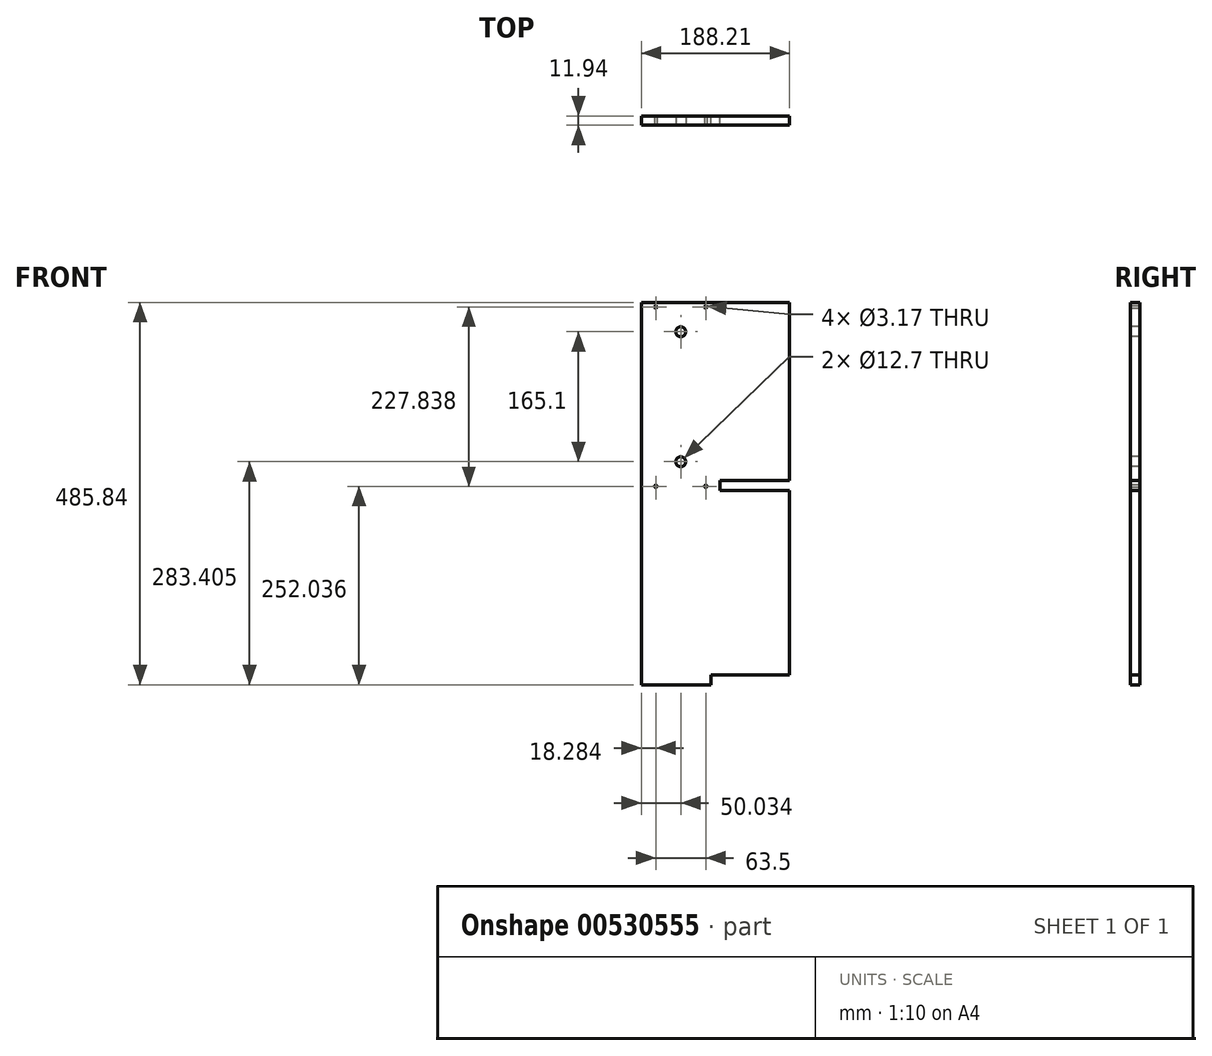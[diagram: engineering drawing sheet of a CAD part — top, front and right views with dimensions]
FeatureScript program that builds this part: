
annotation { "Feature Type Name" : "Feature", "Feature Type Description" : "" }
export const myFeature = defineFeature(function(context is Context, id is Id, definition is map)
    precondition{}
    {
        {
            var Q0;
            Q0=qCreatedBy(makeId("Front.planeOp"),FACE);
            var sketch = newSketch(context, id + "F0", { "sketchPlane" : qUnion([Q0])});
            skLineSegment(sketch, "E0", {"start": v(-136.42, 252.83) * mm, "end": v(-36.35, 252.83) * mm});
            skLineSegment(sketch, "E1", {"start": v(-36.35, 26.52) * mm, "end": v(-36.35, 13.82) * mm});
            skLineSegment(sketch, "E2", {"start": v(-36.35, 13.82) * mm, "end": v(51.79, 13.82) * mm});
            skLineSegment(sketch, "E3", {"start": v(51.79, 13.82) * mm, "end": v(51.79, -220.3) * mm});
            skLineSegment(sketch, "E4", {"start": v(51.79, -220.3) * mm, "end": v(-48.29, -220.3) * mm});
            skLineSegment(sketch, "E5.top", {"start": v(-136.42, -233) * mm, "end": v(-48.29, -233) * mm});
            skLineSegment(sketch, "E5.right", {"start": v(-48.29, -220.3) * mm, "end": v(-48.29, -233) * mm});
            skLineSegment(sketch, "E6.bottom", {"start": v(-36.35, 252.83) * mm, "end": v(51.79, 252.83) * mm});
            skLineSegment(sketch, "E6.top", {"start": v(-36.35, 26.52) * mm, "end": v(51.79, 26.52) * mm});
            skLineSegment(sketch, "E6.right", {"start": v(51.79, 252.83) * mm, "end": v(51.79, 26.52) * mm});
            skPoint(sketch, "E7.start.orphan", {"position": v(-136.42, -220.3) * mm});
            skLineSegment(sketch, "E8", {"start": v(-136.42, 252.83) * mm, "end": v(-136.42, -233) * mm});
            skSolve(sketch);
        }
        {
            var Q0;
            Q0=makeQuery(id+"F0.imprint","IMPRINT",FACE,{"disambiguationData":[TD([[makeQuery(id+"F0.imprint","IMPRINT",EDGE,{"derivedFrom":sQuery(id+"F0.wireOp",EDGE,"E0")}),-1.0]])]});
            extrude(context, id + "F1", {"entities" : qUnion([Q0]), "depth" : 11.94 * mm, "offsetDistance" : 25.4 * mm});
        }
        {
            var Q0;
            Q0=makeQuery(id+"F1.opExtrude","CAP_FACE",FACE,{"disambiguationData":[OSD([sQuery(id+"F0.wireOp",EDGE,"E0"),sQuery(id+"F0.wireOp",EDGE,"E1"),sQuery(id+"F0.wireOp",EDGE,"E2"),sQuery(id+"F0.wireOp",EDGE,"E3"),sQuery(id+"F0.wireOp",EDGE,"E4"),sQuery(id+"F0.wireOp",EDGE,"E5.top"),sQuery(id+"F0.wireOp",EDGE,"E5.right"),sQuery(id+"F0.wireOp",EDGE,"E6.bottom"),sQuery(id+"F0.wireOp",EDGE,"E6.top"),sQuery(id+"F0.wireOp",EDGE,"E6.right"),sQuery(id+"F0.wireOp",EDGE,"E8")])],"isStart":false});
            var sketch = newSketch(context, id + "F2", { "sketchPlane" : qUnion([Q0])});
            skCircle(sketch, "E9", {"center": v(-86.39, 215.5) * mm, "radius": 6.35 * mm});
            skCircle(sketch, "E10", {"center": v(-86.39, 50.4) * mm, "radius": 6.35 * mm});
            skCircle(sketch, "E11", {"center": v(-118.14, 246.86) * mm, "radius": 1.59 * mm});
            skCircle(sketch, "E12", {"center": v(-54.64, 246.86) * mm, "radius": 1.59 * mm});
            skCircle(sketch, "E13", {"center": v(-118.14, 19.03) * mm, "radius": 1.59 * mm});
            skCircle(sketch, "E14", {"center": v(-54.64, 19.03) * mm, "radius": 1.59 * mm});
            skSolve(sketch);
        }
        {
            var Q0;
            Q0 = qSketchRegion(id + "F2", true);
            extrude(context, id + "F3", {"entities" : qUnion([Q0]), "operationType" : NewBodyOperationType.REMOVE, "endBound" : BoundingType.THROUGH_ALL, "oppositeDirection" : true, "depth" : 25.4 * mm, "offsetDistance" : 25.4 * mm});
        }
    });
